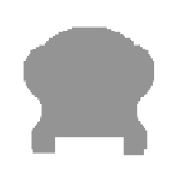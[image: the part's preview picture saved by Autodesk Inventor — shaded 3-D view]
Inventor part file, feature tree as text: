
AUTODESK INVENTOR PART (.ipt)
format: ipt  version: 2019 (Build 230136000, 136)  size: 128,512 bytes
history: native  units: mm
features: other x7, sketch x1, extrude x1
ambient origin geometry x8: Origin, YZ Plane, XZ Plane, XY Plane, X Axis, Y Axis, Z Axis, Center Point
bodies: Body1 (feature_tree)
feature tree (9):
  other  "Твердое тело1"
  other  "Блоки"
  sketch  "Эскиз"
  other  "Начальная плоскость"
  other  "РабПлоскость2"
  extrude  "Тело"  TaperAngle=0.0deg  [1 undecoded]
  other  "Конечная плоскость"
  other  "Поручень"
  other  "Поручень:1"
note: 1 required parameter value undecoded (feature->parameter linkage not recoverable at this tier; creation-order binding heuristic only, values carry confidence <= 0.55)
